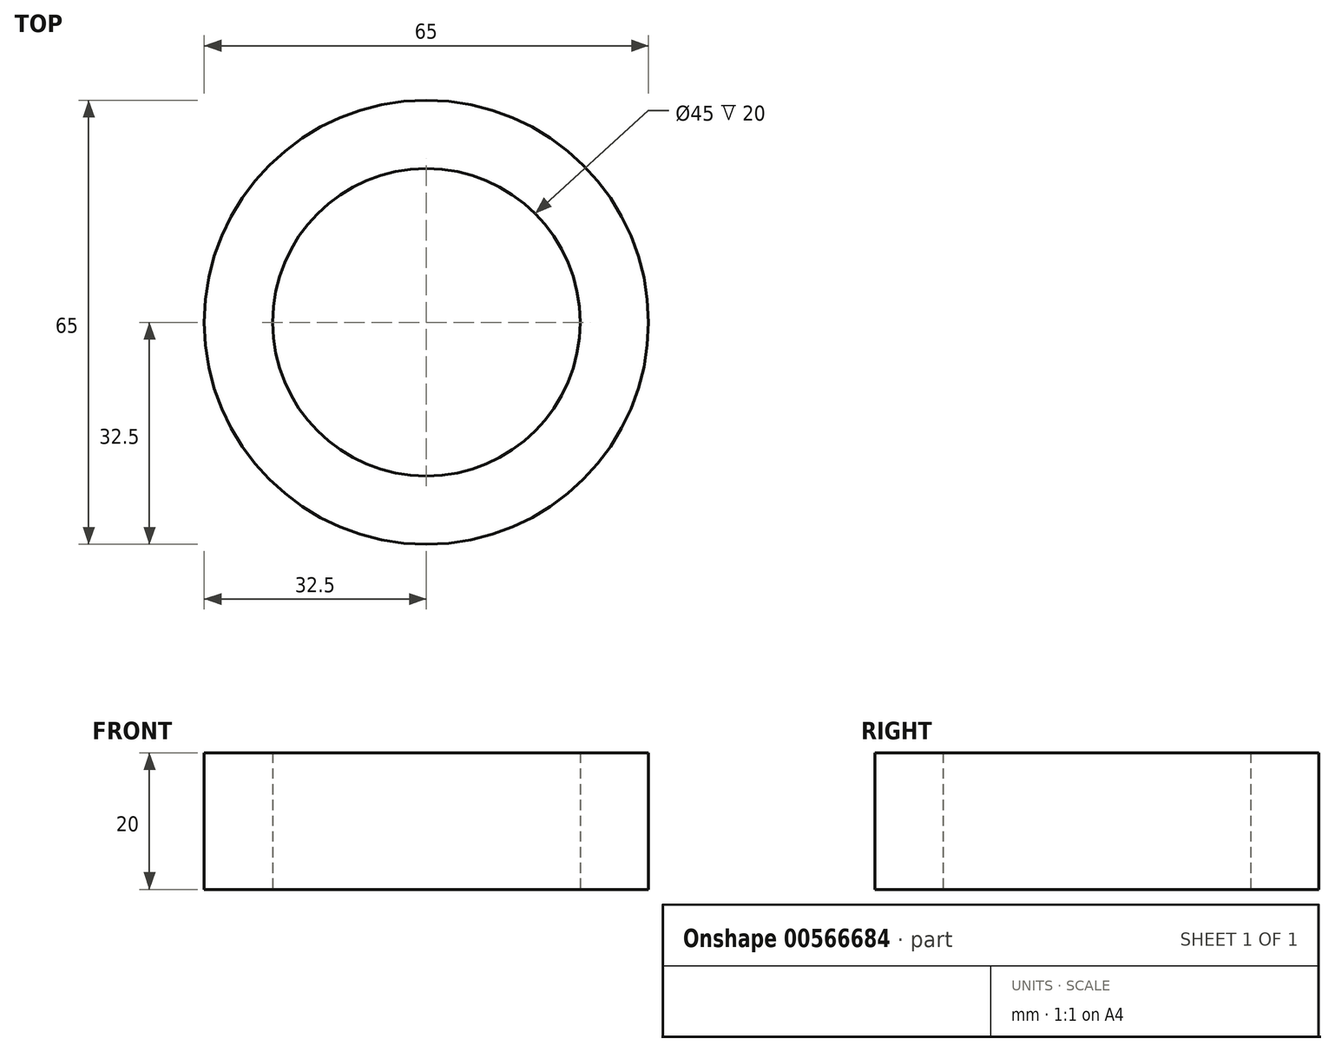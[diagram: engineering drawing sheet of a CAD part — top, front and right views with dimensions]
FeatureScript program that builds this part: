
annotation { "Feature Type Name" : "Feature", "Feature Type Description" : "" }
export const myFeature = defineFeature(function(context is Context, id is Id, definition is map)
    precondition{}
    {
        {
            var Q0;
            Q0=qCreatedBy(makeId("Top.planeOp"),FACE);
            var sketch = newSketch(context, id + "F0", { "sketchPlane" : qUnion([Q0])});
            skCircle(sketch, "E0", {"center": v(0, 0) * mm, "radius": 32.5 * mm});
            skCircle(sketch, "E1", {"center": v(0, 0) * mm, "radius": 22.5 * mm});
            skSolve(sketch);
        }
        {
            var Q0;
            Q0=makeQuery(id+"F0.imprint","IMPRINT",FACE,{"disambiguationData":[TD([[makeQuery(id+"F0.imprint","IMPRINT",EDGE,{"derivedFrom":sQuery(id+"F0.wireOp",EDGE,"E0")}),1.0]])]});
            extrude(context, id + "F1", {"entities" : qUnion([Q0]), "depth" : 20 * mm, "offsetDistance" : 25 * mm});
        }
    });
